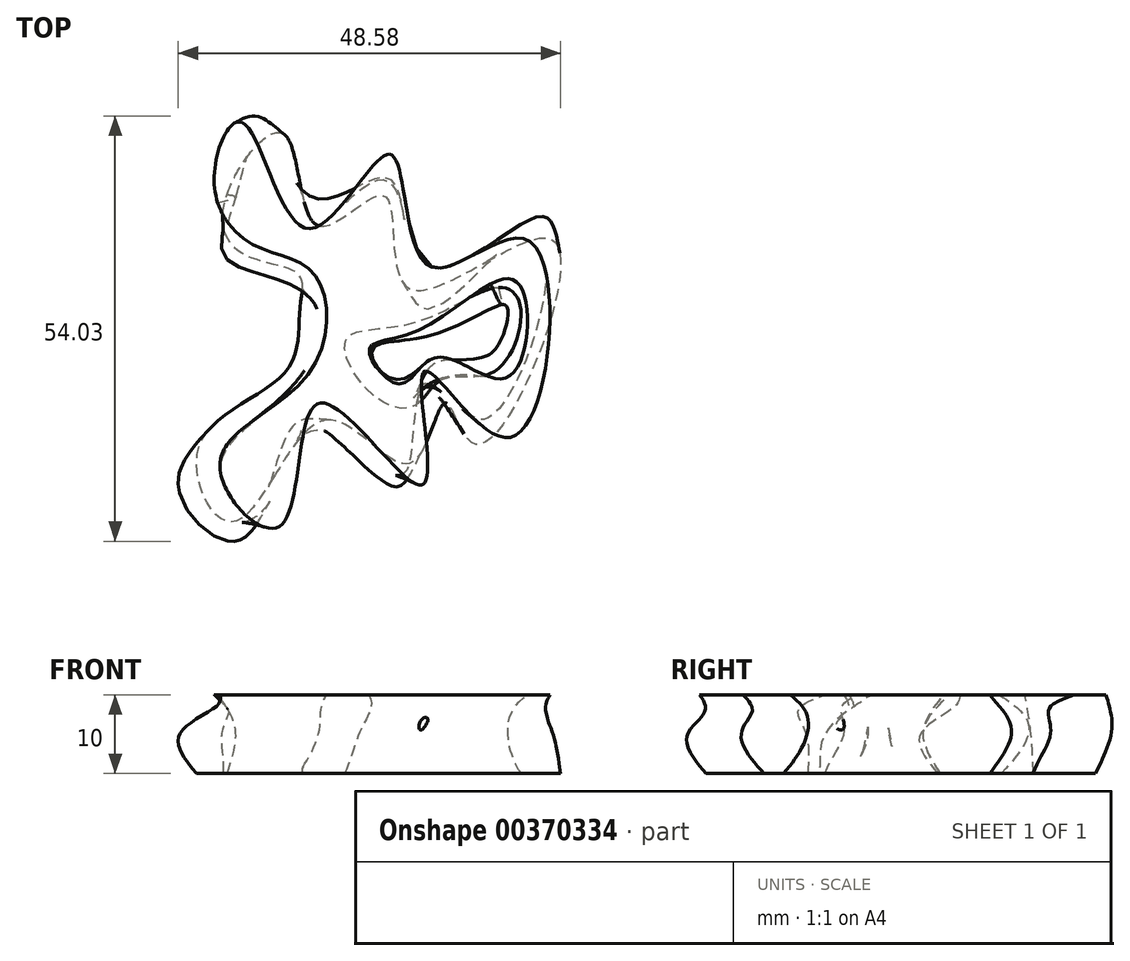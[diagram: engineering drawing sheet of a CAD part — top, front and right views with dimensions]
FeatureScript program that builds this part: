
annotation { "Feature Type Name" : "Feature", "Feature Type Description" : "" }
export const myFeature = defineFeature(function(context is Context, id is Id, definition is map)
    precondition{}
    {
        {
            var Q0;
            Q0=qCreatedBy(makeId("Top.planeOp"),FACE);
            cPlane(context, id + "F0", {"entities" : qUnion([Q0]), "cplaneType" : CPlaneType.OFFSET, "offset" : 5 * mm, "width" : 152.4 * mm, "height" : 152.4 * mm});
        }
        {
            var Q0;
            Q0=qCreatedBy(id+"F0.planeOp",FACE);
            var sketch = newSketch(context, id + "F1", { "sketchPlane" : qUnion([Q0])});
            skFitSpline(sketch, "E0", {"points": [v(-15.13, 14.33) * mm, v(-7.87, 21.96) * mm, v(-3.51, 10.34) * mm, v(4.84, 14.15) * mm, v(8.11, 2.35) * mm, v(26.45, 8.34) * mm, v(16.83, -17.45) * mm, v(12.65, -12.18) * mm, v(8.11, -19.8) * mm, v(-2.6, -14.36) * mm, v(-14.22, -27.25) * mm, v(-18.76, -18) * mm, v(-7.69, -8.19) * mm, v(-5.87, 0) * mm, v(-6.05, 4.16) * mm, v(-13.32, 6.89) * mm, v(-15.13, 14.33) * mm]});
            skSolve(sketch);
        }
        {
            var Q0;
            Q0=qCreatedBy(id+"F0.planeOp",FACE);
            var sketch = newSketch(context, id + "F2", { "sketchPlane" : qUnion([Q0])});
            skFitSpline(sketch, "E1", {"points": [v(19.34, 2.53) * mm, v(22.14, 0) * mm, v(18.7, -8.24) * mm, v(12.17, -9.2) * mm, v(8.71, -12.54) * mm, v(3.1, -10.89) * mm, v(0, -4.07) * mm, v(8.5, -2.02) * mm, v(19.34, 2.53) * mm]});
            skSolve(sketch);
        }
        {
            var Q0;
            Q0=qCreatedBy(id+"F0.planeOp",FACE);
            cPlane(context, id + "F3", {"entities" : qUnion([Q0]), "cplaneType" : CPlaneType.OFFSET, "offset" : 5 * mm, "width" : 152.4 * mm, "height" : 152.4 * mm});
        }
        {
            var Q0;
            Q0=qCreatedBy(id+"F3.planeOp",FACE);
            var sketch = newSketch(context, id + "F4", { "sketchPlane" : qUnion([Q0])});
            skFitSpline(sketch, "E2", {"points": [v(-10.96, 24.14) * mm, v(-3.87, 13.79) * mm, v(5.75, 16.15) * mm, v(10.29, 0) * mm, v(25.36, 11.42) * mm, v(17.37, -14.36) * mm, v(9.93, -9.82) * mm, v(6.84, -22.71) * mm, v(-5.5, -14.54) * mm, v(-12.95, -29.25) * mm, v(-21.12, -22.71) * mm, v(-7.32, -10.36) * mm, v(-3.87, 0) * mm, v(-8.41, 3.44) * mm, v(-15.5, 6.52) * mm, v(-13.86, 14.51) * mm, v(-10.96, 24.14) * mm]});
            skSolve(sketch);
        }
        {
            var Q0;
            Q0=qCreatedBy(id+"F3.planeOp",FACE);
            var sketch = newSketch(context, id + "F5", { "sketchPlane" : qUnion([Q0])});
            skFitSpline(sketch, "E3", {"points": [v(18.82, 0) * mm, v(20.46, 0) * mm, v(17.92, -6.37) * mm, v(11.38, -7.1) * mm, v(8.11, -12) * mm, v(4.3, -9.82) * mm, v(1.76, -4.55) * mm, v(9.2, -3.83) * mm, v(18.82, 0) * mm]});
            skSolve(sketch);
        }
        {
            var Q0;
            Q0=qCreatedBy(id+"F3.planeOp",FACE);
            cPlane(context, id + "F6", {"entities" : qUnion([Q0]), "cplaneType" : CPlaneType.OFFSET, "offset" : 5 * mm, "width" : 152.4 * mm, "height" : 152.4 * mm});
        }
        {
            var Q0;
            Q0=qCreatedBy(id+"F6.planeOp",FACE);
            var sketch = newSketch(context, id + "F7", { "sketchPlane" : qUnion([Q0])});
            skFitSpline(sketch, "E4", {"points": [v(-13.13, 23.4) * mm, v(-4.78, 9.97) * mm, v(5.57, 19.41) * mm, v(10.47, 5.25) * mm, v(23.36, 8.34) * mm, v(20.82, -16.54) * mm, v(9.93, -8.19) * mm, v(9.74, -22.53) * mm, v(-3.33, -12.18) * mm, v(-8.41, -27.8) * mm, v(-16.04, -20.17) * mm, v(-4.96, -8.73) * mm, v(-4.06, 4.16) * mm, v(-11.86, 7.98) * mm, v(-16.77, 16.5) * mm, v(-13.13, 23.4) * mm]});
            skSolve(sketch);
        }
        {
            var Q0;
            Q0=qCreatedBy(id+"F6.planeOp",FACE);
            var sketch = newSketch(context, id + "F8", { "sketchPlane" : qUnion([Q0])});
            skFitSpline(sketch, "E5", {"points": [v(9.2, -2.92) * mm, v(20.82, 3.62) * mm, v(23, -2.74) * mm, v(19.73, -9.1) * mm, v(11.56, -6.37) * mm, v(7.38, -9.64) * mm, v(4.3, -8.19) * mm, v(3.03, -5.1) * mm, v(9.2, -2.92) * mm]});
            skSolve(sketch);
        }
        {
            var Q0;
            Q0=qCreatedBy(id+"F6.planeOp",FACE);
            cPlane(context, id + "F9", {"entities" : qUnion([Q0]), "cplaneType" : CPlaneType.OFFSET, "offset" : 5 * mm, "width" : 152.4 * mm, "height" : 152.4 * mm});
        }
        {
            var Q0;
            Q0=qCreatedBy(id+"F9.planeOp",FACE);
            cPlane(context, id + "F10", {"entities" : qUnion([Q0]), "cplaneType" : CPlaneType.OFFSET, "offset" : 5 * mm, "width" : 152.4 * mm, "height" : 152.4 * mm});
        }
        {
            var Q0;
            Q0=qCreatedBy(id+"F10.planeOp",FACE);
            cPlane(context, id + "F11", {"entities" : qUnion([Q0]), "cplaneType" : CPlaneType.OFFSET, "offset" : 5 * mm, "width" : 152.4 * mm, "height" : 152.4 * mm});
        }
        {
            var Q0;
            Q0=qCreatedBy(id+"F11.planeOp",FACE);
            cPlane(context, id + "F12", {"entities" : qUnion([Q0]), "cplaneType" : CPlaneType.OFFSET, "offset" : 5 * mm, "width" : 152.4 * mm, "height" : 152.4 * mm});
        }
        {
            var Q0;
            Q0=qCreatedBy(id+"F12.planeOp",FACE);
            cPlane(context, id + "F13", {"entities" : qUnion([Q0]), "cplaneType" : CPlaneType.OFFSET, "offset" : 5 * mm, "width" : 152.4 * mm, "height" : 152.4 * mm});
        }
        {
            var Q0;
            Q0=qCreatedBy(id+"F13.planeOp",FACE);
            cPlane(context, id + "F14", {"entities" : qUnion([Q0]), "cplaneType" : CPlaneType.OFFSET, "offset" : 5 * mm, "width" : 152.4 * mm, "height" : 152.4 * mm});
        }
        {
            var Q0;
            Q0=qCreatedBy(id+"F14.planeOp",FACE);
            cPlane(context, id + "F15", {"entities" : qUnion([Q0]), "cplaneType" : CPlaneType.OFFSET, "offset" : 5 * mm, "width" : 152.4 * mm, "height" : 152.4 * mm});
        }
        {
            var Q0;
            Q0=qCreatedBy(id+"F15.planeOp",FACE);
            cPlane(context, id + "F16", {"entities" : qUnion([Q0]), "cplaneType" : CPlaneType.OFFSET, "offset" : 5 * mm, "width" : 152.4 * mm, "height" : 152.4 * mm});
        }
        {
            var Q0;
            Q0=qCreatedBy(id+"F16.planeOp",FACE);
            cPlane(context, id + "F17", {"entities" : qUnion([Q0]), "cplaneType" : CPlaneType.OFFSET, "offset" : 5 * mm, "width" : 152.4 * mm, "height" : 152.4 * mm});
        }
        {
            var Q0;
            Q0=qCreatedBy(id+"F17.planeOp",FACE);
            cPlane(context, id + "F18", {"entities" : qUnion([Q0]), "cplaneType" : CPlaneType.OFFSET, "offset" : 5 * mm, "width" : 152.4 * mm, "height" : 152.4 * mm});
        }
        {
            var Q0;
            Q0 = qSketchRegion(id + "F1", true);
            var Q1;
            Q1 = qSketchRegion(id + "F4", true);
            var Q2;
            Q2 = qSketchRegion(id + "F7", true);
            loft(context, id + "F19", {"sheetProfilesArray" : [{ "sheetProfileEntities" : qUnion([Q0]) }, { "sheetProfileEntities" : qUnion([Q1]) }, { "sheetProfileEntities" : qUnion([Q2]) }]});
        }
        {
            var Q1;
            Q1 = qSketchRegion(id + "F2", true);
            var Q2;
            Q2 = qSketchRegion(id + "F5", true);
            var Q3;
            Q3 = qSketchRegion(id + "F8", true);
            loft(context, id + "F20", {"operationType" : NewBodyOperationType.REMOVE, "sheetProfilesArray" : [{ "sheetProfileEntities" : qUnion([Q1]) }, { "sheetProfileEntities" : qUnion([Q2]) }, { "sheetProfileEntities" : qUnion([Q3]) }]});
        }
    });
